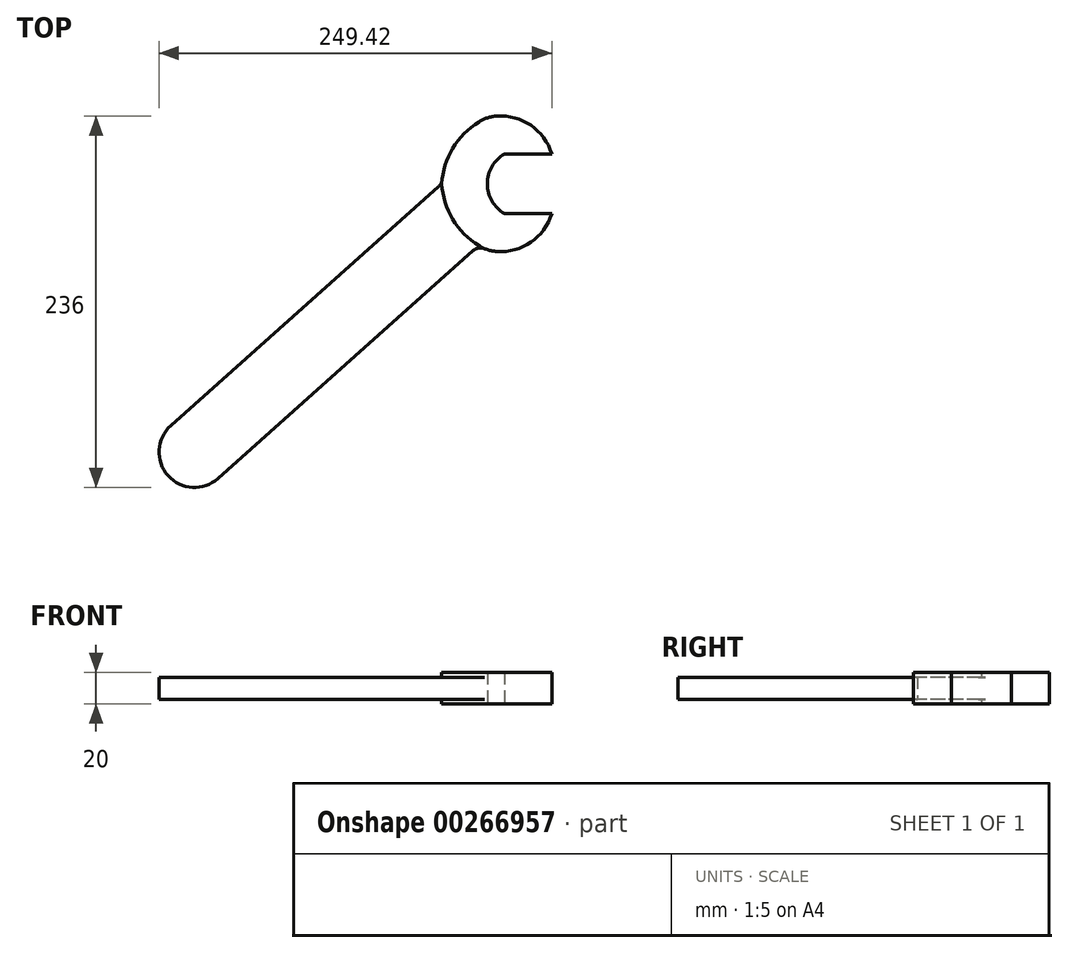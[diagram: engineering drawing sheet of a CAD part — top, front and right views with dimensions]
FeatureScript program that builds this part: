
annotation { "Feature Type Name" : "Feature", "Feature Type Description" : "" }
export const myFeature = defineFeature(function(context is Context, id is Id, definition is map)
    precondition{}
    {
        {
            var Q0;
            Q0=qCreatedBy(makeId("Top.planeOp"),FACE);
            var sketch = newSketch(context, id + "F0", { "sketchPlane" : qUnion([Q0])});
            skLineSegment(sketch, "E0.bottom", {"start": v(35, 0) * mm, "end": v(-35, 0) * mm, "construction": true});
            skLineSegment(sketch, "E0.top", {"start": v(35, 86) * mm, "end": v(-35, 86) * mm, "construction": true});
            skLineSegment(sketch, "E0.left", {"start": v(35, 0) * mm, "end": v(35, 86) * mm, "construction": true});
            skLineSegment(sketch, "E0.right", {"start": v(-35, 0) * mm, "end": v(-35, 43) * mm, "construction": true});
            skPoint(sketch, "E0.middle", {"position": v(0, 43) * mm});
            skLineSegment(sketch, "E1", {"start": v(35, 62) * mm, "end": v(5, 62) * mm});
            skLineSegment(sketch, "E2", {"start": v(35, 24) * mm, "end": v(5, 24) * mm});
            skArc(sketch, "E3", {"start": v(5, 62) * mm, "mid": v(-5.9, 43) * mm, "end": v(5, 24) * mm});
            skLineSegment(sketch, "E4", {"start": v(-66.07, 43) * mm, "end": v(82.25, 43) * mm, "construction": true});
            skArc(sketch, "E5", {"start": v(0, 0) * mm, "mid": v(21.7, 5.87) * mm, "end": v(35, 24) * mm});
            skArc(sketch, "E6", {"start": v(-11.36, 3.69) * mm, "mid": v(-5.9, 1.16) * mm, "end": v(0, 0) * mm});
            skArc(sketch, "E7", {"start": v(-35, 46.18) * mm, "mid": v(-34.97, 44.59) * mm, "end": v(-34.9, 43) * mm, "construction": true});
            skArc(sketch, "E8", {"start": v(-6.74, 99.27) * mm, "mid": v(-27.5, 76.25) * mm, "end": v(-35, 46.18) * mm, "construction": true});
            skPoint(sketch, "E9", {"position": v(0, 0) * mm});
            skLineSegment(sketch, "E10", {"start": v(-35, 43) * mm, "end": v(-35, 86) * mm, "construction": true});
            skArc(sketch, "E11", {"start": v(-34.9, 43) * mm, "mid": v(-27.9, 20.49) * mm, "end": v(-11.36, 3.69) * mm});
            skArc(sketch, "E12.MirrorCS", {"start": v(0, 86) * mm, "mid": v(21.7, 80.13) * mm, "end": v(35, 62) * mm});
            skArc(sketch, "E13.MirrorCS", {"start": v(-34.9, 43) * mm, "mid": v(-27.9, 65.51) * mm, "end": v(-11.36, 82.31) * mm});
            skArc(sketch, "E14.MirrorCS", {"start": v(-11.36, 82.31) * mm, "mid": v(-5.9, 84.84) * mm, "end": v(0, 86) * mm});
            skLineSegment(sketch, "E15", {"start": v(-11.36, 3.69) * mm, "end": v(-176.93, -144.2) * mm});
            skLineSegment(sketch, "E16", {"start": v(-34.9, 43) * mm, "end": v(-206.9, -110.63) * mm});
            skLineSegment(sketch, "E17", {"start": v(-176.93, -144.2) * mm, "end": v(-249.26, -63.22) * mm, "construction": true});
            skArc(sketch, "E18", {"start": v(-206.9, -110.63) * mm, "mid": v(-208.7, -142.4) * mm, "end": v(-176.93, -144.2) * mm});
            skSolve(sketch);
        }
        {
            var Q0;
            Q0=makeQuery(id+"F0.imprint","IMPRINT",FACE,{"disambiguationData":[TD([[makeQuery(id+"F0.imprint","IMPRINT",EDGE,{"derivedFrom":sQuery(id+"F0.wireOp",EDGE,"E11")}),-1.0]])]});
            extrude(context, id + "F1", {"entities" : qUnion([Q0]), "endBound" : BoundingType.SYMMETRIC, "depth" : 14 * mm});
        }
        {
            var Q0;
            Q0=makeQuery(id+"F0.imprint","IMPRINT",FACE,{"disambiguationData":[TD([[makeQuery(id+"F0.imprint","IMPRINT",EDGE,{"derivedFrom":sQuery(id+"F0.wireOp",EDGE,"E1")}),-1.0]])]});
            extrude(context, id + "F2", {"entities" : qUnion([Q0]), "operationType" : NewBodyOperationType.ADD, "endBound" : BoundingType.SYMMETRIC, "depth" : 20 * mm});
        }
        {
            var Q0;
            {var subQ0=sQuery(id+"F0.wireOp",EDGE,"E16");var subQ1=sQuery(id+"F0.wireOp",EDGE,"E13.MirrorCS");var subQ2=sQuery(id+"F0.wireOp",EDGE,"E11");Q0=makeQuery(id+"F2.boolean.opBoolean","MERGE",EDGE,{"derivedFrom":[makeQuery(id+"F1.opExtrude","SWEPT_EDGE",EDGE,{"disambiguationData":[OSD([subQ2,subQ1,subQ0])]}),makeQuery(id+"F2.opExtrude","SWEPT_EDGE",EDGE,{"disambiguationData":[OSD([subQ2,subQ1,subQ0])]})]});}
            var Q1;
            {var subQ0=sQuery(id+"F0.wireOp",EDGE,"E15");var subQ1=sQuery(id+"F0.wireOp",EDGE,"E11");var subQ2=sQuery(id+"F0.wireOp",EDGE,"E6");Q1=makeQuery(id+"F2.boolean.opBoolean","MERGE",EDGE,{"derivedFrom":[makeQuery(id+"F1.opExtrude","SWEPT_EDGE",EDGE,{"disambiguationData":[OSD([subQ2,subQ1,subQ0])]}),makeQuery(id+"F2.opExtrude","SWEPT_EDGE",EDGE,{"disambiguationData":[OSD([subQ2,subQ1,subQ0])]})]});}
            fillet(context, id + "F3", {"entities" : qUnion([Q0, Q1]), "radius" : 7 * mm, "tangentPropagation" : true, "allowEdgeOverflow" : false});
        }
    });
